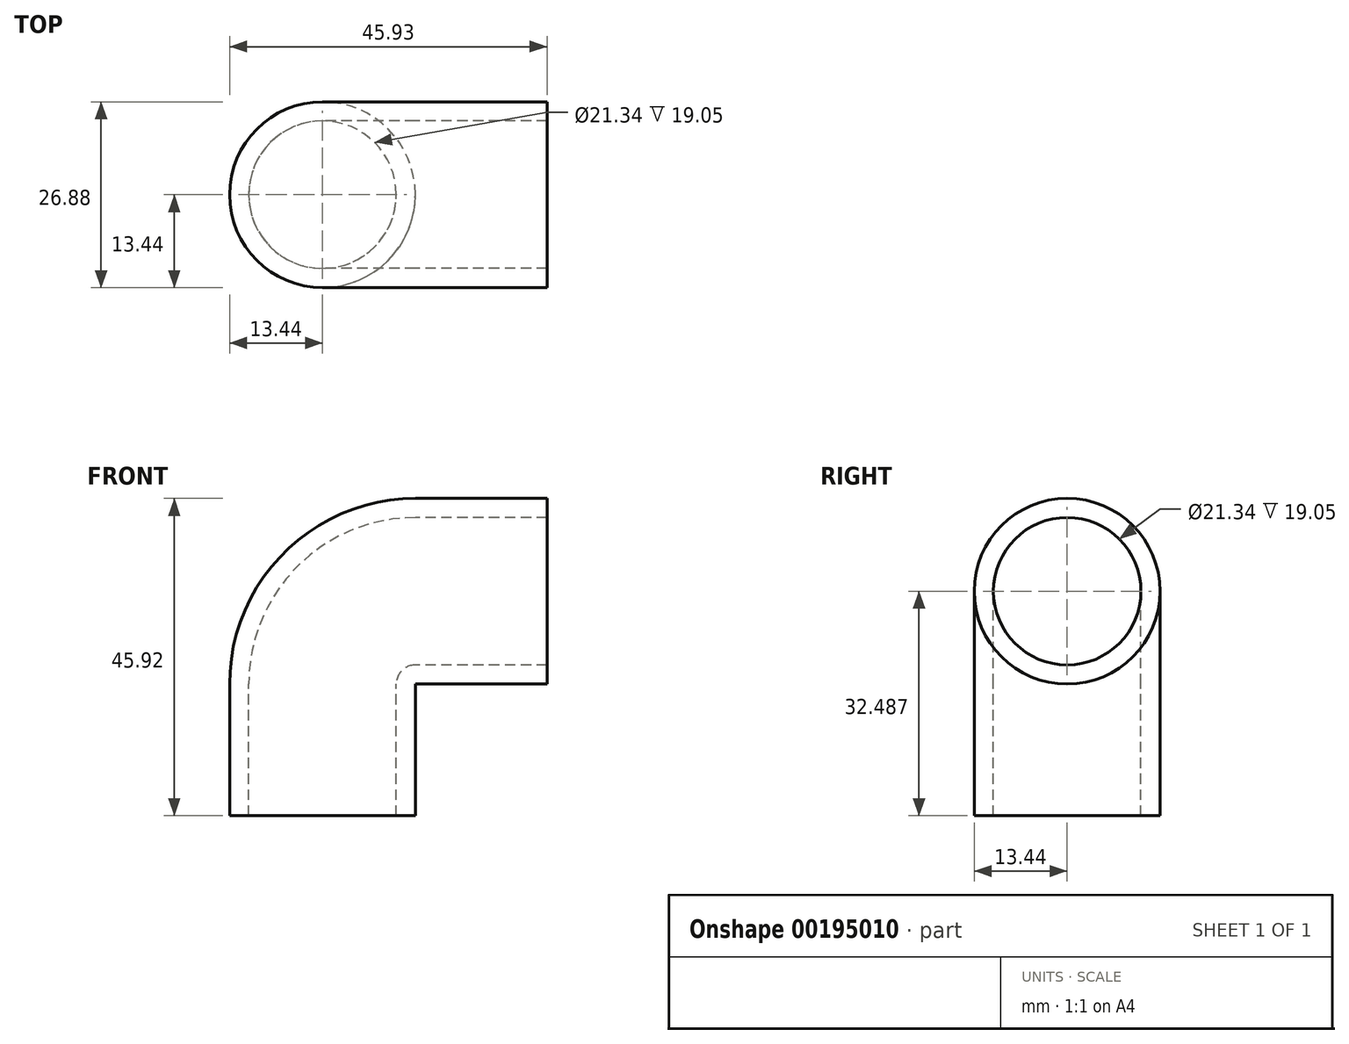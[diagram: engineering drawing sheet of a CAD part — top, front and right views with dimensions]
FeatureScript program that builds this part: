
annotation { "Feature Type Name" : "Feature", "Feature Type Description" : "" }
export const myFeature = defineFeature(function(context is Context, id is Id, definition is map)
    precondition{}
    {
        {
            var Q0;
            Q0=qCreatedBy(makeId("Top.planeOp"),FACE);
            var sketch = newSketch(context, id + "F0", { "sketchPlane" : qUnion([Q0])});
            skCircle(sketch, "E0", {"center": v(0, 0) * mm, "radius": 10.67 * mm});
            skCircle(sketch, "E1", {"center": v(0, 0) * mm, "radius": 13.44 * mm});
            skLineSegment(sketch, "E2", {"start": v(13.44, -14.48) * mm, "end": v(13.44, 17.74) * mm, "construction": true});
            skSolve(sketch);
        }
        {
            var Q0;
            Q0=makeQuery(id+"F0.imprint","IMPRINT",FACE,{"disambiguationData":[TD([[makeQuery(id+"F0.imprint","IMPRINT",EDGE,{"derivedFrom":sQuery(id+"F0.wireOp",EDGE,"E0")}),-1.0]])]});
            extrude(context, id + "F1", {"entities" : qUnion([Q0]), "oppositeDirection" : true, "depth" : 19.05 * mm});
        }
        {
            var Q0;
            Q0=makeQuery(id+"F1.opExtrude","CAP_FACE",FACE,{"disambiguationData":[OSD([sQuery(id+"F0.wireOp",EDGE,"E0"),sQuery(id+"F0.wireOp",EDGE,"E1")])],"isStart":true});
            var Q1;
            Q1=sQuery(id+"F0.wireOp",EDGE,"E2");
            revolve(context, id + "F2", {"operationType" : NewBodyOperationType.ADD, "entities" : qUnion([Q0]), "axis" : qUnion([Q1]), "revolveType" : RevolveType.ONE_DIRECTION, "angle" : 90 * degree});
        }
        {
            var Q0;
            Q0=makeQuery(id+"F2.opRevolve","CAP_FACE",FACE,{"disambiguationData":[OSD([sQuery(id+"F0.wireOp",EDGE,"E0"),sQuery(id+"F0.wireOp",EDGE,"E1")])],"isStart":false});
            extrude(context, id + "F3", {"entities" : qUnion([Q0]), "operationType" : NewBodyOperationType.ADD, "depth" : 19.05 * mm});
        }
    });
